# Revit family: TSL_US - TSLGR45 - Radius ADA Grab Bars
name_source: partatom
category: Specialty Equipment
units: mm (PartAtom-declared; Revit-internal decimal feet)

## family parameters
Always vertical = Yes
Cut with Voids When Loaded = No
Part Type = Normal
Room Calculation Point = No
Round Connector Dimension = Use Diameter
Shared = No
Work Plane-Based = No

## types (24) — shared parameters
Assembly Code = C1030200
Default Elevation = 0' - 0"
Description = A suite of ADA-compliant grab bars made from AISI 304 type stainless steel in a brushed satin finish. Bars are available in 18, 24, 36, and 42-inch lengths.
Keynote = 10 28 00.C1
Manufacturer = The Splash Lab
Type Comments = RADIUS ADA GRAB BARS
Type Image = <None>
URL = https://thesplashlab.com

## per-type parameters (varying)
| type | Model | TSL Material 01 | TSL Width | TSL Width Check | TSL Width Check Half |
| TSL.GR45.42.CS - Satin | TSL.GR45.42.CS | TSL - Material - Satin | 3' - 6" | 3' - 6" | 1' - 9" |
| TSL.GR45.42.CP - Copper | TSL.GR45.42.CP | TSL - Material - Copper | 3' - 6" | 3' - 6" | 1' - 9" |
| TSL.GR45.42.C - Chrome | TSL.GR45.42.C | TSL - Material - Chrome | 3' - 6" | 3' - 6" | 1' - 9" |
| TSL.GR45.42.BR - Brass | TSL.GR45.42.BR | TSL - Material - Brass | 3' - 6" | 3' - 6" | 1' - 9" |
| TSL.GR45.42.BK - Black | TSL.GR45.42.BK | TSL - Material - Black | 3' - 6" | 3' - 6" | 1' - 9" |
| TSL.GR45.36.CS - Satin | TSL.GR45.36.CS | TSL - Material - Satin | 3' - 0" | 3' - 0" | 1' - 6" |
| TSL.GR45.36.CP - Copper | TSL.GR45.36.CP | TSL - Material - Copper | 3' - 0" | 3' - 0" | 1' - 6" |
| TSL.GR45.36.C - Chrome | TSL.GR45.36.C | TSL - Material - Chrome | 3' - 0" | 3' - 0" | 1' - 6" |
| TSL.GR45.36.BR - Brass | TSL.GR45.36.BR | TSL - Material - Brass | 3' - 0" | 3' - 0" | 1' - 6" |
| TSL.GR45.36.BK - Black | TSL.GR45.36.BK | TSL - Material - Black | 3' - 0" | 3' - 0" | 1' - 6" |
| TSL.GR45.24.CS - Satin | TSL.GR45.24.CS | TSL - Material - Satin | 2' - 0" | 2' - 0" | 1' - 0" |
| TSL.GR45.24.CP - Copper | TSL.GR45.24.CP | TSL - Material - Copper | 2' - 0" | 2' - 0" | 1' - 0" |
| TSL.GR45.24.C - Chrome | TSL.GR45.24.C | TSL - Material - Chrome | 2' - 0" | 2' - 0" | 1' - 0" |
| TSL.GR45.24.BR - Brass | TSL.GR45.24.BR | TSL - Material - Brass | 2' - 0" | 2' - 0" | 1' - 0" |
| TSL.GR45.24.BK - Black | TSL.GR45.24.BK | TSL - Material - Black | 2' - 0" | 2' - 0" | 1' - 0" |
| TSL.GR45.18.CS - Satin | TSL.GR45.18.CS | TSL - Material - Satin | 1' - 6" | 1' - 6" | 0' - 9" |
| TSL.GR45.18.CP - Copper | TSL.GR45.18.CP | TSL - Material - Copper | 1' - 6" | 1' - 6" | 0' - 9" |
| TSL.GR45.18.C - Chrome | TSL.GR45.18.C | TSL - Material - Chrome | 1' - 6" | 1' - 6" | 0' - 9" |
| TSL.GR45.18.BR - Brass | TSL.GR45.18.BR | TSL - Material - Brass | 1' - 6" | 1' - 6" | 0' - 9" |
| TSL.GR45.18.BK - Black | TSL.GR45.18.BK | TSL - Material - Black | 1' - 6" | 1' - 6" | 0' - 9" |
| TSL.GR45.42.BZ - Bronze | TSL.GR45.42.BZ | TSL - Material - Bronze | 3' - 6" | 3' - 6" | 1' - 9" |
| TSL.GR45.36.BZ - Bronze | TSL.GR45.36.BZ | TSL - Material - Bronze | 3' - 0" | 3' - 0" | 1' - 6" |
| TSL.GR45.24.BZ - Bronze | TSL.GR45.24.BZ | TSL - Material - Bronze | 2' - 0" | 2' - 0" | 1' - 0" |
| TSL.GR45.18.BZ - Bronze | TSL.GR45.18.BZ | TSL - Material - Bronze | 1' - 6" | 1' - 6" | 0' - 9" |

## geometry (parser evidence)
native form markers: Sweep x6
no freeform markers — native parametric forms only
